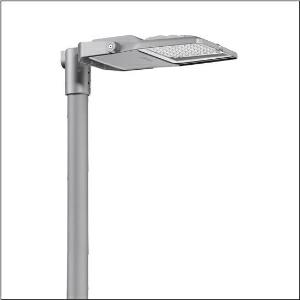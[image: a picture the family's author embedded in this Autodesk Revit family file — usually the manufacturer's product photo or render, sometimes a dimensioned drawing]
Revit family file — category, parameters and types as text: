
# Revit family: floodlight_fl_21_iq_mini___pl61_5xa7772d2c3a_9c70
name_source: partatom
category: Lighting Fixtures
units: mm (PartAtom-declared; Revit-internal decimal feet)

## family parameters
Cut with Voids When Loaded = No
Host = Face
Light Source = No
Part Type = Normal
Room Calculation Point = No
Round Connector Dimension = Use Diameter
Shared = No

## types (1)
- --- (1 x LED, 17500 lm, 143 W, 3000K)
    Apparent Load = 143 VA
    CIE Flux Codes = 33 65 98 100 100
    Color Rendering = 70
    Color Temperature = 3000K
    Default Elevation = 1800 mm
    Description = Floodlight FL 21 iQ mini, floodlight, primary light control with lens, of PMMA, primary optical cover: protective disc, of toughened safety glass, transparent, light distribution: PL61, light emission: direct distribution, installation type: surface-mounted, LED, High Power LED, rated luminous flux: 17.500lm, luminous efficacy: 122lm/W, light colour: 730, colour temperature: 3000K, control: Auto-Match, Temp-Guard, Night-Set, Smart-Wire, Desk-Remote (wireless, voltage-free reading and setting of iQ features in the workshop via application-optimized NFC function/RFID function), optimised constant luminous flux control (CLO 2.0), Light-Fading, Lumen-Switch, with terminal, 6-pole, mains connection: 220..240V, AC, 50/60Hz, start of lifetime: 143W, end of service life: 152W, reduction: 61W, luminaire housing, of diecast aluminium, powder-coated, Siteco® metallic grey (DB 702S), corrosivity category C5 mid according to DIN EN ISO 12944, sealing non-destructively replaceable, please order mast flange separately, mast bracket, of steel, galvanised, powder-coated, protection rating (complete): IP66, insulation class (complete): insulation class II (safety insulation), certification: CE, ENEC, VDE, protection symbol: D, impact resistance: IK08, permissible operating ambient temperature: -40..+40°C, permissible operating ambient temperature for outdoor applications: -40..+50°C, standard: DIN EN 12944, LABS conformity tested according to VDMA 24364:2018-05, packaging unit: 1 piece

Light Distribution: PL61
    Height = 70 mm
    Lamp = 1 x LED
    Lamp Light Flux = 17500 lm
    Lamp Power = 143 W
    Lamp count = 1
    Length = 485 mm
    Luminous efficacy = 122 lm/W
    Manufacturer = Siteco
    ModVariant = No
    Model = 5XA7772D2C3A
    Number of Poles = 1
    OnlyDefault = Yes
    Power Factor = 1
    Product Name = Floodlight FL 21 iQ mini | PL61
    Product group = floodlight | pylon annexe
    ProductGroupID = 6200
    Protection Class = Protection class II
    Protection Degree = IP 66
    RLX_Detail_Level = 1
    RLX_Emergency_Light_Flux = 0 lm
    RLX_Emergency_Type = 0
    RLX_Emergency_Type_DB = No
    RlxData = <blob elided: 101573 chars, md5=2e7318f1>
    Socket = socket
    Standby Power = 0 W
    System Light Flux = 17500 lm
    System Power = 143 W
    Type Comments = factory setting: luminous flux: 100 % | dim-lin: 254 | 730 mA
    Type Image = l_1007125.jpg
    URL = http://relux.com
    VarID = @adj_123379
    Voltage = 0 V
    Weight = 0.00 kg
    Width = 337 mm

## geometry (parser evidence)
native form markers: Blend x4, Sweep x11
no freeform markers — native parametric forms only
